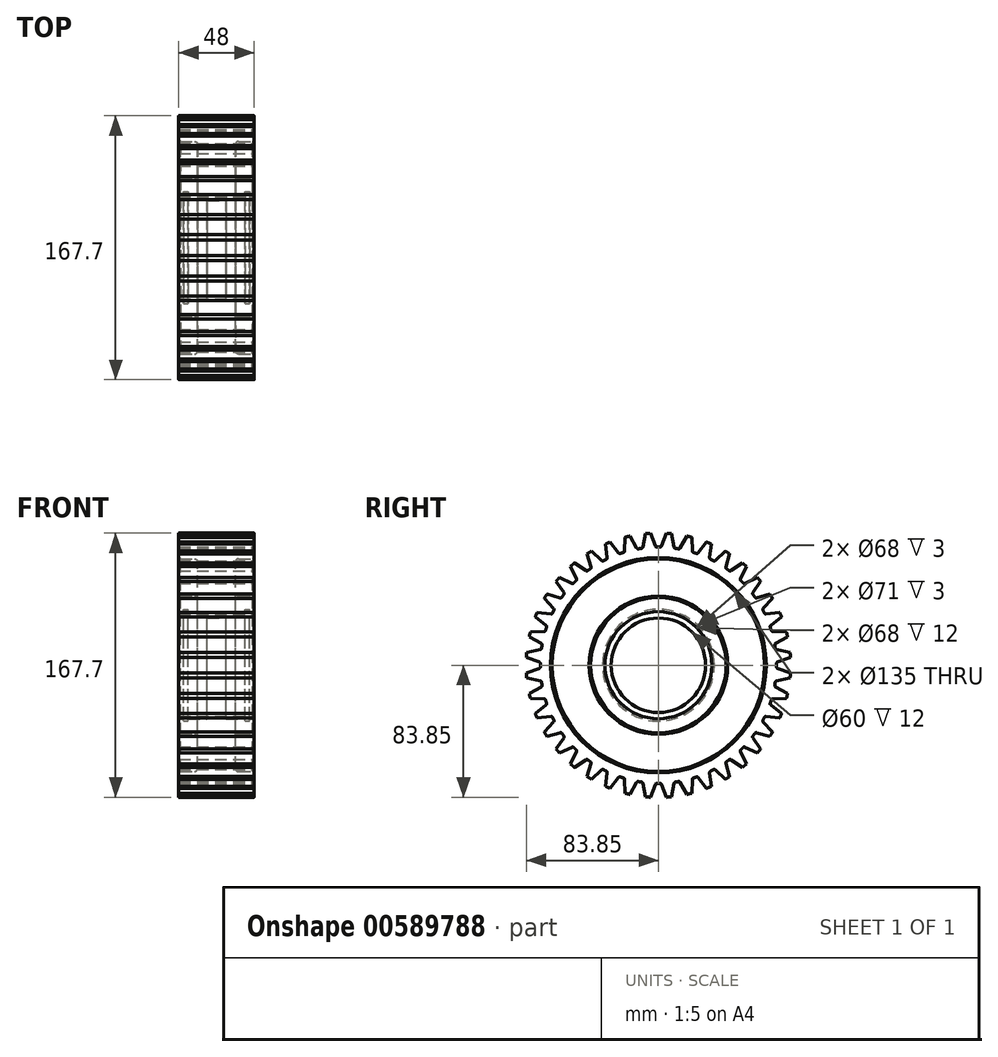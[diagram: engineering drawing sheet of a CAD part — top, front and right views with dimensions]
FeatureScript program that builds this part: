
annotation { "Feature Type Name" : "Feature", "Feature Type Description" : "" }
export const myFeature = defineFeature(function(context is Context, id is Id, definition is map)
    precondition{}
    {
        {
            var Q0;
            Q0=qCreatedBy(makeId("Front.planeOp"),FACE);
            var sketch = newSketch(context, id + "F0", { "sketchPlane" : qUnion([Q0])});
            skLineSegment(sketch, "E0.top", {"start": v(0, 84) * mm, "end": v(-24, 84) * mm});
            skLineSegment(sketch, "E0.right", {"start": v(-24, 34) * mm, "end": v(-24, 44) * mm});
            skLineSegment(sketch, "E1", {"start": v(-24, 34) * mm, "end": v(-21, 34) * mm});
            skLineSegment(sketch, "E2", {"start": v(-21, 34) * mm, "end": v(-21, 35.5) * mm});
            skLineSegment(sketch, "E3", {"start": v(-21, 35.5) * mm, "end": v(-18, 35.5) * mm});
            skLineSegment(sketch, "E4", {"start": v(-18, 35.5) * mm, "end": v(-18, 34) * mm});
            skLineSegment(sketch, "E5", {"start": v(-6, 34) * mm, "end": v(-6, 30) * mm});
            skLineSegment(sketch, "E6", {"start": v(-6, 30) * mm, "end": v(0, 30) * mm});
            skLineSegment(sketch, "E7", {"start": v(-18, 34) * mm, "end": v(-6, 34) * mm});
            skLineSegment(sketch, "E8", {"start": v(-24, 44) * mm, "end": v(-14, 44) * mm});
            skLineSegment(sketch, "E9", {"start": v(-12, 46) * mm, "end": v(-12, 65.5) * mm});
            skLineSegment(sketch, "E10", {"start": v(-14, 67.5) * mm, "end": v(-24, 67.5) * mm});
            skLineSegment(sketch, "E11.trimOffspring", {"start": v(-24, 67.5) * mm, "end": v(-24, 84) * mm});
            skPoint(sketch, "E12.visualSharp", {"position": v(-12, 67.5) * mm});
            skArc(sketch, "E12.filletArc", {"start": v(-12, 65.5) * mm, "mid": v(-12.59, 66.91) * mm, "end": v(-14, 67.5) * mm});
            skPoint(sketch, "E13.visualSharp", {"position": v(-12, 44) * mm});
            skArc(sketch, "E13.filletArc", {"start": v(-14, 44) * mm, "mid": v(-12.59, 44.59) * mm, "end": v(-12, 46) * mm});
            skLineSegment(sketch, "E14.MirrorCS", {"start": v(0, 84) * mm, "end": v(24, 84) * mm});
            skLineSegment(sketch, "E15.MirrorCS", {"start": v(24, 67.5) * mm, "end": v(24, 84) * mm});
            skLineSegment(sketch, "E16.MirrorCS", {"start": v(14, 67.5) * mm, "end": v(24, 67.5) * mm});
            skArc(sketch, "E17.MirrorCS", {"start": v(12, 65.5) * mm, "mid": v(12.59, 66.91) * mm, "end": v(14, 67.5) * mm});
            skLineSegment(sketch, "E18.MirrorCS", {"start": v(12, 46) * mm, "end": v(12, 65.5) * mm});
            skArc(sketch, "E19.MirrorCS", {"start": v(14, 44) * mm, "mid": v(12.59, 44.59) * mm, "end": v(12, 46) * mm});
            skLineSegment(sketch, "E20.MirrorCS", {"start": v(24, 44) * mm, "end": v(14, 44) * mm});
            skLineSegment(sketch, "E21.MirrorCS", {"start": v(24, 34) * mm, "end": v(24, 44) * mm});
            skLineSegment(sketch, "E22.MirrorCS", {"start": v(24, 34) * mm, "end": v(21, 34) * mm});
            skLineSegment(sketch, "E23.MirrorCS", {"start": v(21, 34) * mm, "end": v(21, 35.5) * mm});
            skLineSegment(sketch, "E24.MirrorCS", {"start": v(21, 35.5) * mm, "end": v(18, 35.5) * mm});
            skLineSegment(sketch, "E25.MirrorCS", {"start": v(18, 35.5) * mm, "end": v(18, 34) * mm});
            skLineSegment(sketch, "E26.MirrorCS", {"start": v(18, 34) * mm, "end": v(6, 34) * mm});
            skLineSegment(sketch, "E27.MirrorCS", {"start": v(6, 34) * mm, "end": v(6, 30) * mm});
            skLineSegment(sketch, "E28.MirrorCS", {"start": v(6, 30) * mm, "end": v(0, 30) * mm});
            skLineSegment(sketch, "E29", {"start": v(0, 0) * mm, "end": v(-27, 0) * mm});
            skSolve(sketch);
        }
        {
            var Q0;
            Q0=makeQuery(id+"F0.imprint","IMPRINT",FACE,{"disambiguationData":[TD([[makeQuery(id+"F0.imprint","IMPRINT",EDGE,{"derivedFrom":sQuery(id+"F0.wireOp",EDGE,"E0.top")}),1.0]])]});
            var Q1;
            Q1=sQuery(id+"F0.wireOp",EDGE,"E29");
            revolve(context, id + "F1", {"entities" : qUnion([Q0]), "axis" : qUnion([Q1]), "revolveType" : RevolveType.FULL});
        }
        {
            var Q0;
            Q0=qCreatedBy(makeId("Right.planeOp"),FACE);
            var sketch = newSketch(context, id + "F2", { "sketchPlane" : qUnion([Q0])});
            skArc(sketch, "E30", {"start": v(1.04, 75) * mm, "mid": v(0, 75) * mm, "end": v(-1.04, 75) * mm});
            skLineSegment(sketch, "E31", {"start": v(0, 0) * mm, "end": v(0, 84) * mm, "construction": true});
            skArc(sketch, "E32.0", {"start": v(4.98, 83.85) * mm, "mid": v(0, 84) * mm, "end": v(-4.98, 83.85) * mm});
            skLineSegment(sketch, "E33", {"start": v(2, 75.65) * mm, "end": v(4.98, 83.85) * mm});
            skLineSegment(sketch, "E34.MirrorCS", {"start": v(-2, 75.65) * mm, "end": v(-4.98, 83.85) * mm});
            skPoint(sketch, "E35.visualSharp", {"position": v(-1.75, 74.98) * mm});
            skArc(sketch, "E35.filletArc", {"start": v(-2, 75.65) * mm, "mid": v(-1.62, 75.17) * mm, "end": v(-1.04, 75) * mm});
            skPoint(sketch, "E36.visualSharp", {"position": v(1.75, 74.98) * mm});
            skArc(sketch, "E36.filletArc", {"start": v(1.04, 75) * mm, "mid": v(1.62, 75.17) * mm, "end": v(2, 75.65) * mm});
            skSolve(sketch);
        }
        {
            var Q0;
            Q0 = qSketchRegion(id + "F2", true);
            extrude(context, id + "F3", {"entities" : qUnion([Q0]), "operationType" : NewBodyOperationType.REMOVE, "oppositeDirection" : true, "depth" : 75 * mm, "offsetDistance" : 25 * mm, "symmetric" : true});
        }
        {
            var Q0;
            Q0=makeQuery(id+"F3.boolean.opBoolean","COPY",FACE,{"derivedFrom":makeQuery(id+"F3.opExtrude","SWEPT_FACE",FACE,{"disambiguationData":[OSD([sQuery(id+"F2.wireOp",EDGE,"E33")])]})});
            var Q1;
            Q1=makeQuery(id+"F3.boolean.opBoolean","COPY",FACE,{"derivedFrom":makeQuery(id+"F3.opExtrude","SWEPT_FACE",FACE,{"disambiguationData":[OSD([sQuery(id+"F2.wireOp",EDGE,"E36.filletArc")])]})});
            var Q2;
            Q2=makeQuery(id+"F3.boolean.opBoolean","COPY",FACE,{"derivedFrom":makeQuery(id+"F3.opExtrude","SWEPT_FACE",FACE,{"disambiguationData":[OSD([sQuery(id+"F2.wireOp",EDGE,"E30")])]})});
            var Q3;
            Q3=makeQuery(id+"F3.boolean.opBoolean","COPY",FACE,{"derivedFrom":makeQuery(id+"F3.opExtrude","SWEPT_FACE",FACE,{"disambiguationData":[OSD([sQuery(id+"F2.wireOp",EDGE,"E35.filletArc")])]})});
            var Q4;
            Q4=makeQuery(id+"F3.boolean.opBoolean","COPY",FACE,{"derivedFrom":makeQuery(id+"F3.opExtrude","SWEPT_FACE",FACE,{"disambiguationData":[OSD([sQuery(id+"F2.wireOp",EDGE,"E34.MirrorCS")])]})});
            var Q5;
            Q5=makeQuery(id+"F1.opRevolve","SWEPT_FACE",FACE,{"disambiguationData":[OSD([sQuery(id+"F0.wireOp",EDGE,"E0.top"),sQuery(id+"F0.wireOp",EDGE,"E14.MirrorCS")])]});
            circularPattern(context, id + "F4", {"patternType" : PatternType.FACE, "faces" : qUnion([Q0, Q1, Q2, Q3, Q4]), "axis" : qUnion([Q5]), "angle" : 9 * degree, "instanceCount" : 40, "isCentered" : true});
        }
        {
            var Q0;
            Q0=makeQuery(id+"F1.opRevolve","SWEPT_EDGE",EDGE,{"disambiguationData":[OSD([sQuery(id+"F0.wireOp",EDGE,"E15.MirrorCS"),sQuery(id+"F0.wireOp",EDGE,"E16.MirrorCS")])]});
            var Q1;
            Q1=makeQuery(id+"F1.opRevolve","SWEPT_EDGE",EDGE,{"disambiguationData":[OSD([sQuery(id+"F0.wireOp",EDGE,"E20.MirrorCS"),sQuery(id+"F0.wireOp",EDGE,"E21.MirrorCS")])]});
            var Q2;
            Q2=makeQuery(id+"F1.opRevolve","SWEPT_EDGE",EDGE,{"disambiguationData":[OSD([sQuery(id+"F0.wireOp",EDGE,"E0.right"),sQuery(id+"F0.wireOp",EDGE,"E8")])]});
            var Q3;
            Q3=makeQuery(id+"F1.opRevolve","SWEPT_EDGE",EDGE,{"disambiguationData":[OSD([sQuery(id+"F0.wireOp",EDGE,"E10"),sQuery(id+"F0.wireOp",EDGE,"E11.trimOffspring")])]});
            chamfer(context, id + "F5", {"entities" : qUnion([Q0, Q1, Q2, Q3]), "chamferType" : ChamferType.OFFSET_ANGLE, "width" : 1 * mm, "oppositeDirection" : false, "angle" : 45 * degree, "tangentPropagation" : true});
        }
    });
